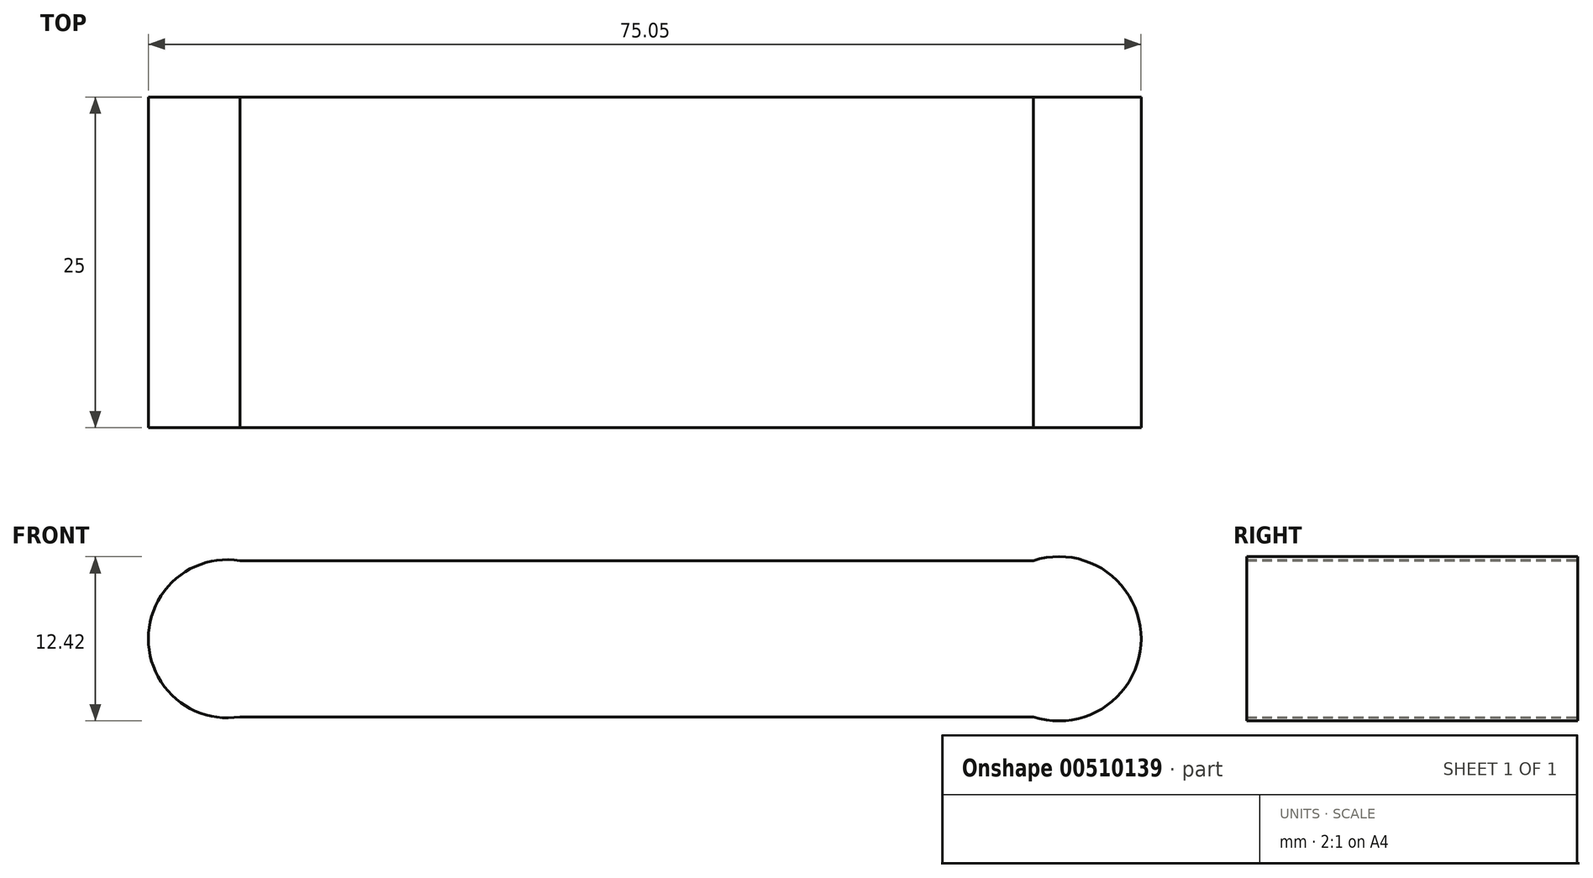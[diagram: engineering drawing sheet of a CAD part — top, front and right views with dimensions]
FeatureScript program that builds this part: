
annotation { "Feature Type Name" : "Feature", "Feature Type Description" : "" }
export const myFeature = defineFeature(function(context is Context, id is Id, definition is map)
    precondition{}
    {
        {
            var Q0;
            Q0=qCreatedBy(makeId("Front.planeOp"),FACE);
            var sketch = newSketch(context, id + "F0", { "sketchPlane" : qUnion([Q0])});
            skLineSegment(sketch, "E0.bottom", {"start": v(-34, 5.87) * mm, "end": v(26, 5.87) * mm});
            skLineSegment(sketch, "E0.top", {"start": v(-34, -5.94) * mm, "end": v(26, -5.94) * mm});
            skLineSegment(sketch, "E0.left", {"start": v(-34, 5.87) * mm, "end": v(-34, -5.94) * mm});
            skLineSegment(sketch, "E0.right", {"start": v(26, 5.87) * mm, "end": v(26, -5.94) * mm});
            skArc(sketch, "E1", {"start": v(-34, 5.87) * mm, "mid": v(-40.92, -0.04) * mm, "end": v(-34, -5.94) * mm});
            skArc(sketch, "E2", {"start": v(26, -5.94) * mm, "mid": v(34.13, -0.04) * mm, "end": v(26, 5.87) * mm});
            skSolve(sketch);
        }
        {
            var Q0;
            Q0 = qSketchRegion(id + "F0", true);
            extrude(context, id + "F1", {"entities" : qUnion([Q0]), "depth" : 25 * mm});
        }
    });
